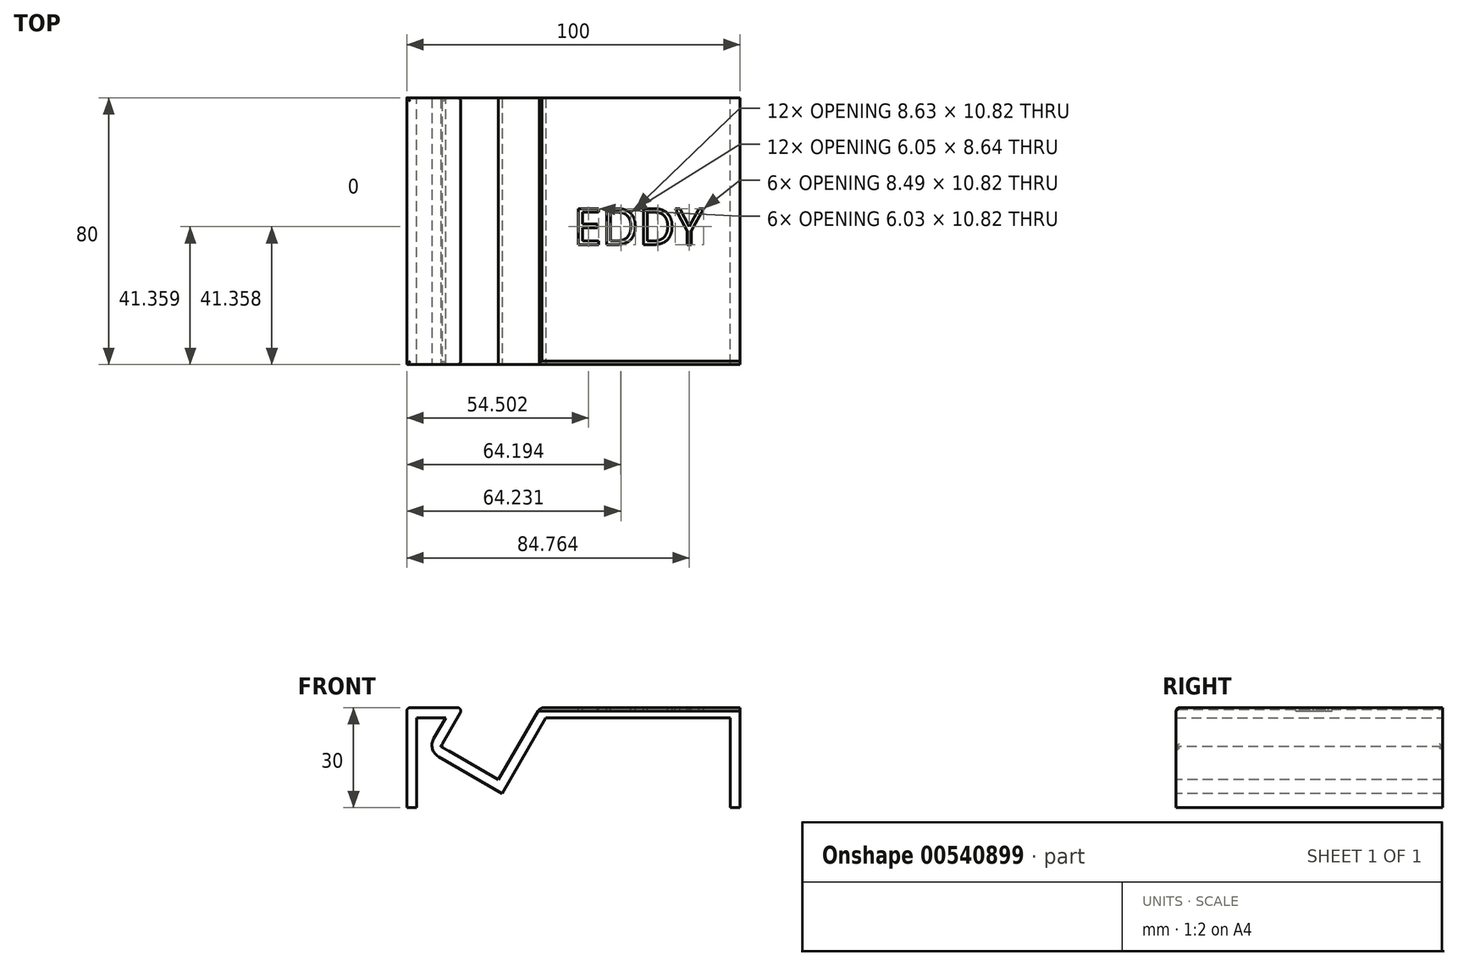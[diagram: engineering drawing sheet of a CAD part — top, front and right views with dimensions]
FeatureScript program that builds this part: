
annotation { "Feature Type Name" : "Feature", "Feature Type Description" : "" }
export const myFeature = defineFeature(function(context is Context, id is Id, definition is map)
    precondition{}
    {
        {
            var Q0;
            Q0=qCreatedBy(makeId("Top.planeOp"),FACE);
            var sketch = newSketch(context, id + "F0", { "sketchPlane" : qUnion([Q0])});
            skLineSegment(sketch, "E0.bottom", {"start": v(50, -40) * mm, "end": v(-50, -40) * mm});
            skLineSegment(sketch, "E0.top", {"start": v(50, 40) * mm, "end": v(-50, 40) * mm});
            skLineSegment(sketch, "E0.left", {"start": v(50, -40) * mm, "end": v(50, 40) * mm});
            skLineSegment(sketch, "E0.right", {"start": v(-50, -40) * mm, "end": v(-50, 40) * mm});
            skPoint(sketch, "E0.middle", {"position": v(0, 0) * mm});
            skSolve(sketch);
        }
        {
            var Q0;
            Q0=makeQuery(id+"F0.imprint","IMPRINT",FACE,{"disambiguationData":[TD([[makeQuery(id+"F0.imprint","IMPRINT",EDGE,{"derivedFrom":sQuery(id+"F0.wireOp",EDGE,"E0.bottom")}),-1.0]])]});
            extrude(context, id + "F1", {"entities" : qUnion([Q0]), "depth" : 30 * mm, "offsetDistance" : 25 * mm});
        }
        {
            var Q0;
            Q0=makeQuery(id+"F1.opExtrude","SWEPT_FACE",FACE,{"disambiguationData":[OSD([sQuery(id+"F0.wireOp",EDGE,"E0.bottom")])]});
            var sketch = newSketch(context, id + "F2", { "sketchPlane" : qUnion([Q0])});
            skLineSegment(sketch, "E1.bottom", {"start": v(-39.82, 18.35) * mm, "end": v(-27.32, 40) * mm});
            skLineSegment(sketch, "E1.top", {"start": v(-22.5, 8.35) * mm, "end": v(-10, 30) * mm});
            skLineSegment(sketch, "E1.left", {"start": v(-39.82, 18.35) * mm, "end": v(-22.5, 8.35) * mm});
            skLineSegment(sketch, "E1.right", {"start": v(-27.32, 40) * mm, "end": v(-10, 30) * mm});
            skSolve(sketch);
        }
        {
            var Q0;
            {var subQ4=sQuery(id+"F2.wireOp",EDGE,"E1.top");Q0=makeQuery(id+"F2.imprint","IMPRINT",FACE,{"disambiguationData":[TD([[makeQuery(id+"F2.imprint","IMPRINT",EDGE,{"derivedFrom":subQ4}),1.0]])]});}
            extrude(context, id + "F3", {"entities" : qUnion([Q0]), "operationType" : NewBodyOperationType.REMOVE, "oppositeDirection" : true, "depth" : 80 * mm, "offsetDistance" : 25 * mm});
        }
        {
            var Q0;
            Q0=makeQuery(id+"F3.boolean.opBoolean","COPY",EDGE,{"derivedFrom":makeQuery(id+"F3.opExtrude","SWEPT_EDGE",EDGE,{"disambiguationData":[OSD([sQuery(id+"F0.wireOp",EDGE,"E0.bottom"),sQuery(id+"F2.wireOp",EDGE,"E1.top"),sQuery(id+"F2.wireOp",EDGE,"E1.right")])]})});
            chamfer(context, id + "F4", {"entities" : qUnion([Q0]), "width" : 1 * mm, "tangentPropagation" : true});
        }
        {
            var Q0;
            Q0=makeQuery(id+"F3.boolean.opBoolean","COPY",EDGE,{"derivedFrom":makeQuery(id+"F3.opExtrude","SWEPT_EDGE",EDGE,{"disambiguationData":[OSD([sQuery(id+"F0.wireOp",EDGE,"E0.bottom"),sQuery(id+"F2.wireOp",EDGE,"E1.bottom")])]})});
            var Q1;
            {var subQ0=sQuery(id+"F0.wireOp",EDGE,"E0.bottom");var subQ1=sQuery(id+"F0.wireOp",EDGE,"E0.right");Q1=makeQuery(id+"F3.boolean.opBoolean","SPLIT",EDGE,{"disambiguationData":[TD([makeQuery(id+"F1.opExtrude","SWEPT_FACE",FACE,{"disambiguationData":[OSD([subQ1])]})])],"derivedFrom":makeQuery(id+"F1.opExtrude","CAP_EDGE",EDGE,{"disambiguationData":[OSD([subQ0])],"isStart":false})});}
            var Q2;
            Q2=makeQuery(id+"F1.opExtrude","CAP_EDGE",EDGE,{"disambiguationData":[OSD([sQuery(id+"F0.wireOp",EDGE,"E0.right")])],"isStart":false});
            var Q3;
            {var subQ0=sQuery(id+"F0.wireOp",EDGE,"E0.right");var subQ1=sQuery(id+"F0.wireOp",EDGE,"E0.top");Q3=makeQuery(id+"F3.boolean.opBoolean","SPLIT",EDGE,{"disambiguationData":[TD([makeQuery(id+"F1.opExtrude","SWEPT_FACE",FACE,{"disambiguationData":[OSD([subQ0])]})])],"derivedFrom":makeQuery(id+"F1.opExtrude","CAP_EDGE",EDGE,{"disambiguationData":[OSD([subQ1])],"isStart":false})});}
            var Q4;
            Q4=makeQuery(id+"F3.boolean.opBoolean","COPY",FACE,{"derivedFrom":makeQuery(id+"F3.opExtrude","SWEPT_FACE",FACE,{"disambiguationData":[OSD([sQuery(id+"F2.wireOp",EDGE,"E1.bottom")])]})});
            var Q5;
            Q5=makeQuery(id+"F3.boolean.opBoolean","COPY",EDGE,{"derivedFrom":makeQuery(id+"F3.opExtrude","CAP_EDGE",EDGE,{"disambiguationData":[OSD([sQuery(id+"F2.wireOp",EDGE,"E1.top")])],"isStart":true})});
            var Q6;
            Q6=makeQuery(id+"F3.boolean.opBoolean","COPY",EDGE,{"derivedFrom":makeQuery(id+"F3.opExtrude","CAP_EDGE",EDGE,{"disambiguationData":[OSD([sQuery(id+"F2.wireOp",EDGE,"E1.top")])],"isStart":false})});
            fillet(context, id + "F5", {"entities" : qUnion([Q0, Q1, Q2, Q3, Q4, Q5, Q6]), "radius" : 1 * mm, "tangentPropagation" : true, "allowEdgeOverflow" : false});
        }
        {
            var Q0;
            Q0=makeQuery(id+"F1.opExtrude","CAP_FACE",FACE,{"disambiguationData":[OSD([sQuery(id+"F0.wireOp",EDGE,"E0.bottom"),sQuery(id+"F0.wireOp",EDGE,"E0.top"),sQuery(id+"F0.wireOp",EDGE,"E0.left"),sQuery(id+"F0.wireOp",EDGE,"E0.right")])],"isStart":true});
            var Q1;
            Q1=makeQuery(id+"F1.opExtrude","SWEPT_FACE",FACE,{"disambiguationData":[OSD([sQuery(id+"F0.wireOp",EDGE,"E0.bottom")])]});
            var Q2;
            Q2=makeQuery(id+"F1.opExtrude","SWEPT_FACE",FACE,{"disambiguationData":[OSD([sQuery(id+"F0.wireOp",EDGE,"E0.top")])]});
            shell(context, id + "F6", {"entities" : qUnion([Q0, Q1, Q2]), "thickness" : 3 * mm});
        }
        {
            var Q0;
            {var subQ0=sQuery(id+"F0.wireOp",EDGE,"E0.bottom");var subQ1=sQuery(id+"F0.wireOp",EDGE,"E0.left");Q0=makeQuery(id+"F3.boolean.opBoolean","SPLIT",EDGE,{"disambiguationData":[TD([makeQuery(id+"F1.opExtrude","SWEPT_FACE",FACE,{"disambiguationData":[OSD([subQ1])]})])],"derivedFrom":makeQuery(id+"F1.opExtrude","CAP_EDGE",EDGE,{"disambiguationData":[OSD([subQ0])],"isStart":false})});}
            chamfer(context, id + "F7", {"entities" : qUnion([Q0]), "width" : 1 * mm, "tangentPropagation" : true});
        }
        {
            var Q0;
            {var subQ0=sQuery(id+"F0.wireOp",EDGE,"E0.bottom");var subQ1=sQuery(id+"F0.wireOp",EDGE,"E0.top");var subQ2=sQuery(id+"F0.wireOp",EDGE,"E0.left");Q0=makeQuery(id+"F3.boolean.opBoolean","SPLIT",FACE,{"disambiguationData":[TD([makeQuery(id+"F1.opExtrude","SWEPT_FACE",FACE,{"disambiguationData":[OSD([subQ2])]})])],"derivedFrom":makeQuery(id+"F1.opExtrude","CAP_FACE",FACE,{"disambiguationData":[OSD([subQ0,subQ1,subQ2,sQuery(id+"F0.wireOp",EDGE,"E0.right")])],"isStart":false})});}
            var sketch = newSketch(context, id + "F8", { "sketchPlane" : qUnion([Q0])});
            skText(sketch, "E2", { "text": "EDDY\n\n\n", "fontName": "OpenSans-Regular.ttf"});
            const initialGuessF8  = {"E2": [0, -0.00405, 1, 0, 0.01091]};
            skSetInitialGuess(sketch, initialGuessF8);
            skSolve(sketch);
        }
        {
            var Q0;
            Q0 = qSketchRegion(id + "F8", true);
            extrude(context, id + "F9", {"entities" : qUnion([Q0]), "operationType" : NewBodyOperationType.REMOVE, "oppositeDirection" : true, "depth" : 1 * mm, "offsetDistance" : 25 * mm});
        }
    });
